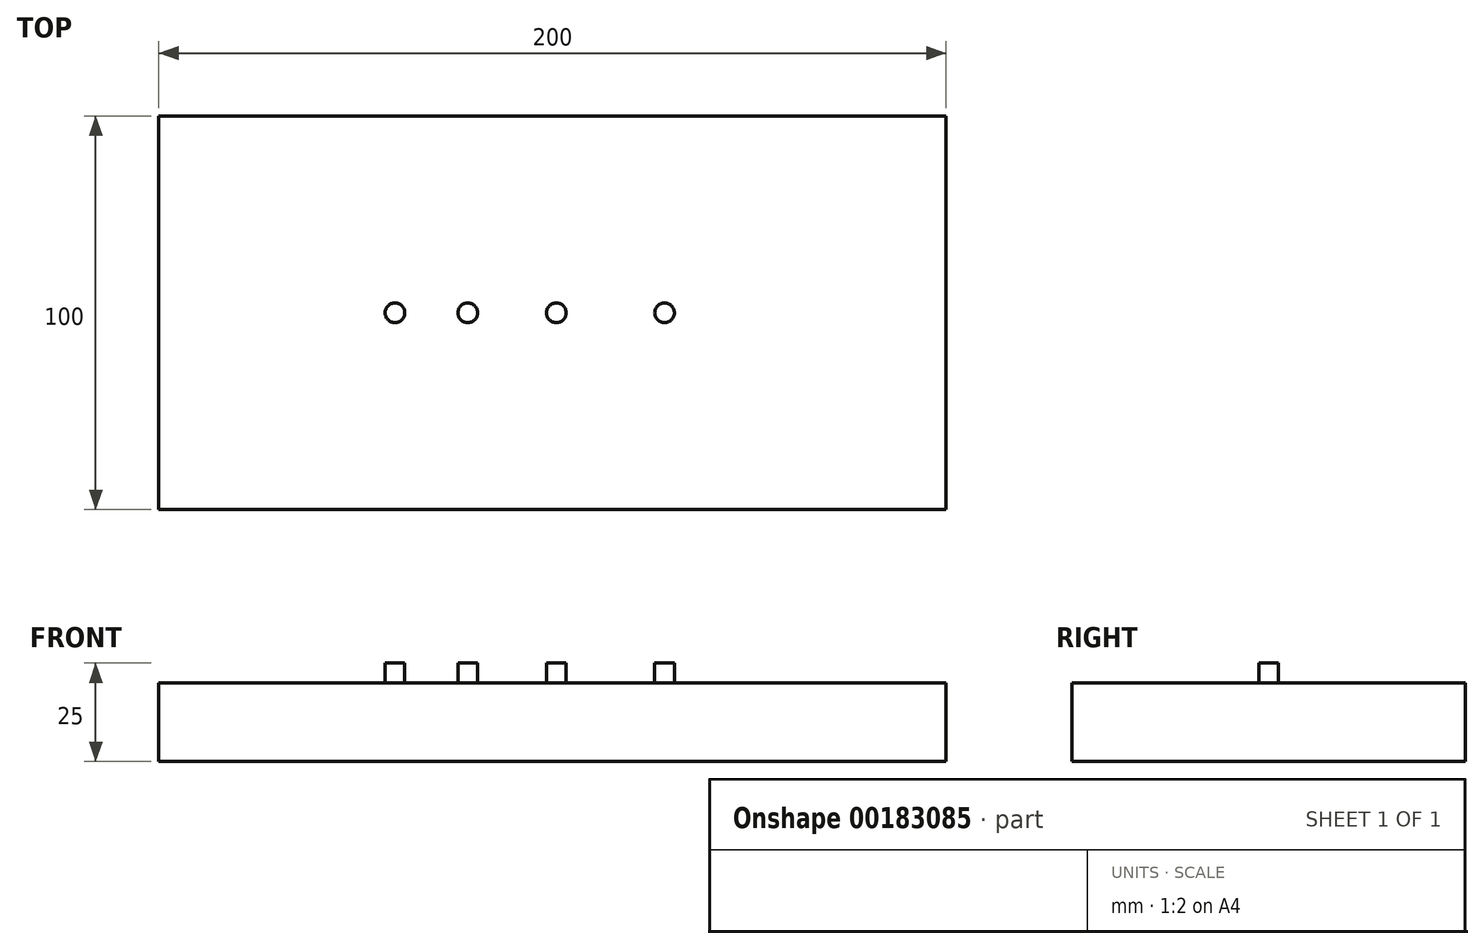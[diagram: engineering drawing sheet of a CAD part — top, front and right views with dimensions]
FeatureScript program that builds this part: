
annotation { "Feature Type Name" : "Feature", "Feature Type Description" : "" }
export const myFeature = defineFeature(function(context is Context, id is Id, definition is map)
    precondition{}
    {
        {
            var Q0;
            Q0=qCreatedBy(makeId("Top.planeOp"),FACE);
            var sketch = newSketch(context, id + "F0", { "sketchPlane" : qUnion([Q0])});
            skLineSegment(sketch, "E0.bottom", {"start": v(-100, 50) * mm, "end": v(100, 50) * mm});
            skLineSegment(sketch, "E0.top", {"start": v(-100, -50) * mm, "end": v(100, -50) * mm});
            skLineSegment(sketch, "E0.left", {"start": v(-100, 50) * mm, "end": v(-100, -50) * mm});
            skLineSegment(sketch, "E0.right", {"start": v(100, 50) * mm, "end": v(100, -50) * mm});
            skSolve(sketch);
        }
        {
            var Q0;
            Q0=makeQuery(id+"F0.imprint","IMPRINT",FACE,{"disambiguationData":[TD([[makeQuery(id+"F0.imprint","IMPRINT",EDGE,{"derivedFrom":sQuery(id+"F0.wireOp",EDGE,"E0.bottom")}),-1.0]])]});
            extrude(context, id + "F1", {"entities" : qUnion([Q0]), "depth" : 20 * mm});
        }
        {
            var Q0;
            Q0=makeQuery(id+"F1.opExtrude","CAP_FACE",FACE,{"disambiguationData":[OSD([sQuery(id+"F0.wireOp",EDGE,"E0.bottom"),sQuery(id+"F0.wireOp",EDGE,"E0.top"),sQuery(id+"F0.wireOp",EDGE,"E0.left"),sQuery(id+"F0.wireOp",EDGE,"E0.right")])],"isStart":false});
            var sketch = newSketch(context, id + "F2", { "sketchPlane" : qUnion([Q0])});
            skCircle(sketch, "E1", {"center": v(-40, 0) * mm, "radius": 2.5 * mm});
            skCircle(sketch, "E2", {"center": v(-21.5, 0) * mm, "radius": 2.5 * mm});
            skCircle(sketch, "E3", {"center": v(1, 0) * mm, "radius": 2.5 * mm});
            skCircle(sketch, "E4", {"center": v(28.5, 0) * mm, "radius": 2.5 * mm});
            skSolve(sketch);
        }
        {
            var Q0;
            Q0 = qSketchRegion(id + "F2", true);
            extrude(context, id + "F3", {"entities" : qUnion([Q0]), "operationType" : NewBodyOperationType.ADD, "depth" : 5 * mm});
        }
    });
